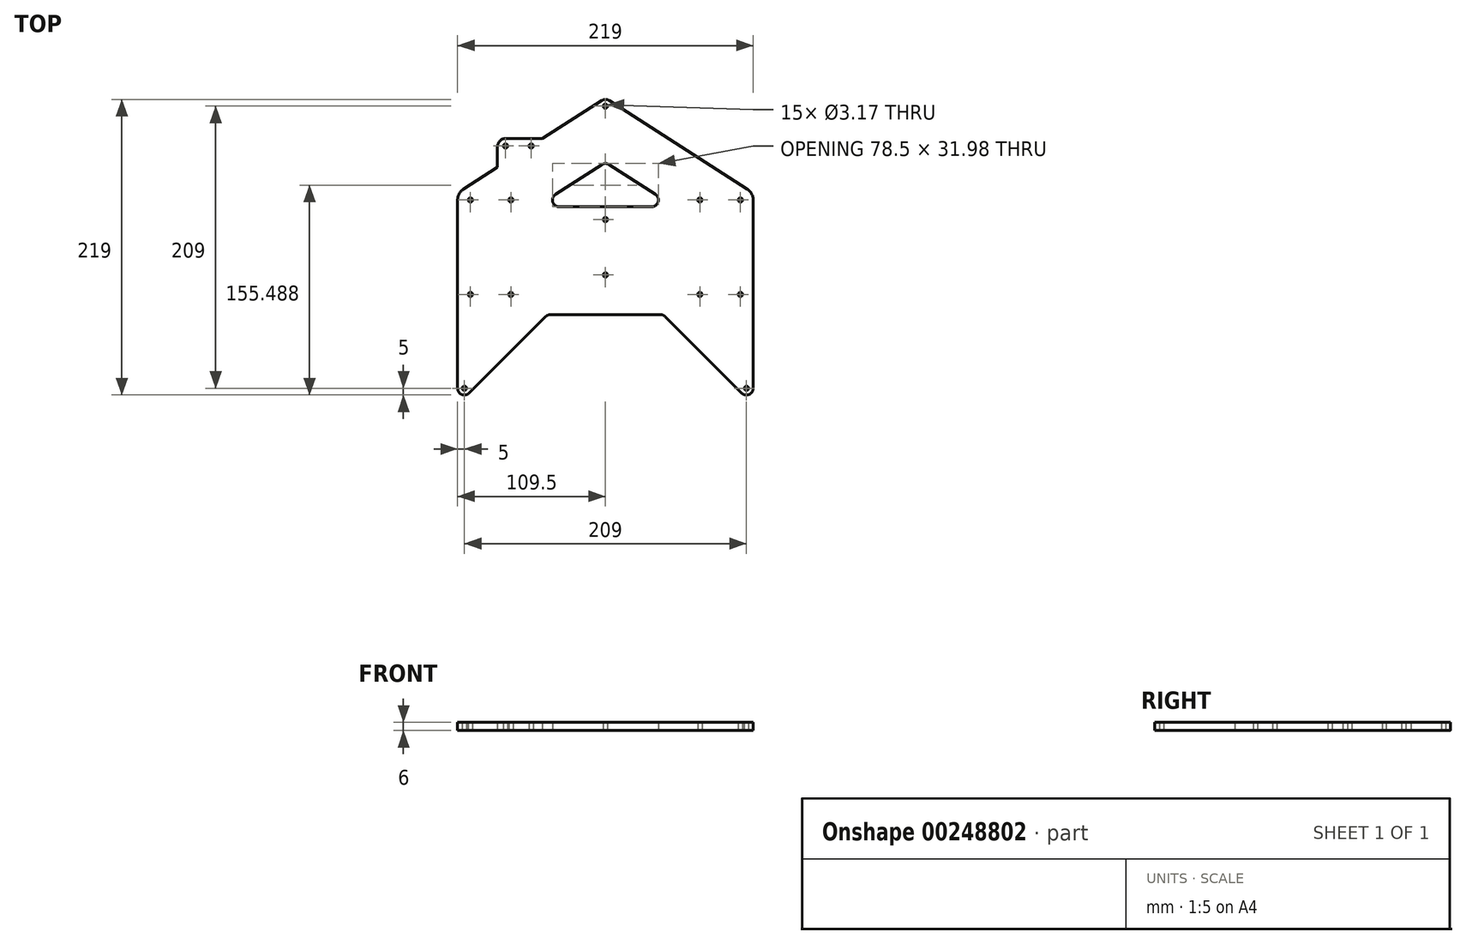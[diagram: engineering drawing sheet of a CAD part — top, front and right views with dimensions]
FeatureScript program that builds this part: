
annotation { "Feature Type Name" : "Feature", "Feature Type Description" : "" }
export const myFeature = defineFeature(function(context is Context, id is Id, definition is map)
    precondition{}
    {
        {
            var Q0;
            Q0=qCreatedBy(makeId("Top.planeOp"),FACE);
            var sketch = newSketch(context, id + "F0", { "sketchPlane" : qUnion([Q0])});
            skCircle(sketch, "E0", {"center": v(0, 20.5) * mm, "radius": 1.59 * mm});
            skCircle(sketch, "E1.MirrorC", {"center": v(0, -20.5) * mm, "radius": 1.59 * mm});
            skLineSegment(sketch, "E2", {"start": v(-100, 35) * mm, "end": v(-70, 35) * mm, "construction": true});
            skPoint(sketch, "E3", {"position": v(-85, 35) * mm});
            skCircle(sketch, "E4", {"center": v(-100, 35) * mm, "radius": 1.59 * mm});
            skCircle(sketch, "E5", {"center": v(-70, 35) * mm, "radius": 1.59 * mm});
            skCircle(sketch, "E6.MirrorC", {"center": v(-70, -35) * mm, "radius": 1.59 * mm});
            skCircle(sketch, "E7.MirrorC", {"center": v(-100, -35) * mm, "radius": 1.59 * mm});
            skLineSegment(sketch, "E8.MirrorCS", {"start": v(-100, -35) * mm, "end": v(-70, -35) * mm, "construction": true});
            skPoint(sketch, "E9.MirrorP", {"position": v(-85, -35) * mm});
            skCircle(sketch, "E10", {"center": v(-104.5, -104.5) * mm, "radius": 1.59 * mm});
            skCircle(sketch, "E11", {"center": v(0, 104.5) * mm, "radius": 1.59 * mm});
            skCircle(sketch, "E12.MirrorC", {"center": v(104.5, -104.5) * mm, "radius": 1.59 * mm});
            skArc(sketch, "E13", {"start": v(-109.5, -104.5) * mm, "mid": v(-106.41, -109.12) * mm, "end": v(-100.96, -108.04) * mm});
            skLineSegment(sketch, "E14", {"start": v(-109.5, -104.5) * mm, "end": v(-109.5, 35) * mm});
            skArc(sketch, "E15", {"start": v(-2.7, 108.7) * mm, "mid": v(-1.4, 109.3) * mm, "end": v(0, 109.5) * mm});
            skArc(sketch, "E16", {"start": v(-109.5, 35) * mm, "mid": v(-108.34, 39.56) * mm, "end": v(-105.13, 43) * mm});
            skLineSegment(sketch, "E17", {"start": v(-105.13, 43) * mm, "end": v(-80, 59.12) * mm});
            skPoint(sketch, "E18.orphan", {"position": v(-5, 104.5) * mm});
            skLineSegment(sketch, "E19", {"start": v(-100.96, -108.04) * mm, "end": v(-44.4, -51.46) * mm});
            skLineSegment(sketch, "E20", {"start": v(-40.86, -50) * mm, "end": v(0, -50) * mm});
            skArc(sketch, "E21.MirrorCS", {"start": v(2.7, 108.7) * mm, "mid": v(1.4, 109.3) * mm, "end": v(0, 109.5) * mm});
            skCircle(sketch, "E22.MirrorC", {"center": v(100, 35) * mm, "radius": 1.59 * mm});
            skCircle(sketch, "E23.MirrorC", {"center": v(70, 35) * mm, "radius": 1.59 * mm});
            skCircle(sketch, "E24.MirrorC", {"center": v(70, -35) * mm, "radius": 1.59 * mm});
            skCircle(sketch, "E25.MirrorC", {"center": v(100, -35) * mm, "radius": 1.59 * mm});
            skArc(sketch, "E26.MirrorCS", {"start": v(109.5, 35) * mm, "mid": v(108.34, 39.56) * mm, "end": v(105.13, 43) * mm});
            skArc(sketch, "E27.MirrorCS", {"start": v(109.5, -104.5) * mm, "mid": v(106.41, -109.12) * mm, "end": v(100.96, -108.04) * mm});
            skLineSegment(sketch, "E28.MirrorCS", {"start": v(40.86, -50) * mm, "end": v(0, -50) * mm});
            skLineSegment(sketch, "E29.MirrorCS", {"start": v(100, -35) * mm, "end": v(70, -35) * mm, "construction": true});
            skLineSegment(sketch, "E30.MirrorCS", {"start": v(100, 35) * mm, "end": v(70, 35) * mm, "construction": true});
            skPoint(sketch, "E31.MirrorP", {"position": v(5, 104.5) * mm});
            skLineSegment(sketch, "E32.MirrorCS", {"start": v(109.5, -104.5) * mm, "end": v(109.5, 35) * mm});
            skLineSegment(sketch, "E33.MirrorCS", {"start": v(105.13, 43) * mm, "end": v(2.7, 108.7) * mm});
            skPoint(sketch, "E34.MirrorP", {"position": v(85, 35) * mm});
            skPoint(sketch, "E35.MirrorP", {"position": v(85, -35) * mm});
            skLineSegment(sketch, "E36.MirrorCS", {"start": v(100.96, -108.04) * mm, "end": v(44.4, -51.46) * mm});
            skPoint(sketch, "E37.visualSharp", {"position": v(-42.93, -50) * mm});
            skArc(sketch, "E37.filletArc", {"start": v(-40.86, -50) * mm, "mid": v(-42.77, -50.38) * mm, "end": v(-44.4, -51.46) * mm});
            skPoint(sketch, "E38.visualSharp", {"position": v(42.93, -50) * mm});
            skArc(sketch, "E38.filletArc", {"start": v(44.4, -51.46) * mm, "mid": v(42.77, -50.38) * mm, "end": v(40.86, -50) * mm});
            skLineSegment(sketch, "E39", {"start": v(0, 30) * mm, "end": v(-34.26, 30) * mm});
            skLineSegment(sketch, "E40", {"start": v(-36.96, 39.2) * mm, "end": v(-2.7, 61.18) * mm});
            skLineSegment(sketch, "E41.MirrorCS", {"start": v(36.96, 39.2) * mm, "end": v(2.7, 61.18) * mm});
            skLineSegment(sketch, "E42.MirrorCS", {"start": v(0, 30) * mm, "end": v(34.26, 30) * mm});
            skPoint(sketch, "E43.visualSharp", {"position": v(0, 62.92) * mm});
            skArc(sketch, "E43.filletArc", {"start": v(2.7, 61.18) * mm, "mid": v(0, 61.98) * mm, "end": v(-2.7, 61.18) * mm});
            skPoint(sketch, "E44.visualSharp", {"position": v(-51.3, 30) * mm});
            skArc(sketch, "E44.filletArc", {"start": v(-36.96, 39.2) * mm, "mid": v(-39.05, 33.6) * mm, "end": v(-34.26, 30) * mm});
            skPoint(sketch, "E45.visualSharp", {"position": v(51.3, 30) * mm});
            skArc(sketch, "E45.filletArc", {"start": v(34.26, 30) * mm, "mid": v(39.05, 33.6) * mm, "end": v(36.96, 39.2) * mm});
            skLineSegment(sketch, "E46", {"start": v(-46.67, 80.5) * mm, "end": v(-74, 80.5) * mm});
            skLineSegment(sketch, "E47", {"start": v(-80, 74.5) * mm, "end": v(-80, 59.12) * mm});
            skLineSegment(sketch, "E48.trimOffspring", {"start": v(-46.67, 80.5) * mm, "end": v(-2.7, 108.7) * mm});
            skCircle(sketch, "E49", {"center": v(-55, 75) * mm, "radius": 1.59 * mm});
            skCircle(sketch, "E50", {"center": v(-74, 75) * mm, "radius": 1.59 * mm});
            skPoint(sketch, "E51.visualSharp", {"position": v(-80, 80.5) * mm});
            skArc(sketch, "E51.filletArc", {"start": v(-74, 80.5) * mm, "mid": v(-78.24, 78.74) * mm, "end": v(-80, 74.5) * mm});
            skSolve(sketch);
        }
        {
            var Q0;
            Q0=makeQuery(id+"F0.imprint","IMPRINT",FACE,{"disambiguationData":[TD([[makeQuery(id+"F0.imprint","IMPRINT",EDGE,{"derivedFrom":sQuery(id+"F0.wireOp",EDGE,"E0")}),-1.0]])]});
            extrude(context, id + "F1", {"entities" : qUnion([Q0]), "depth" : 6 * mm, "offsetDistance" : 25 * mm});
        }
    });
